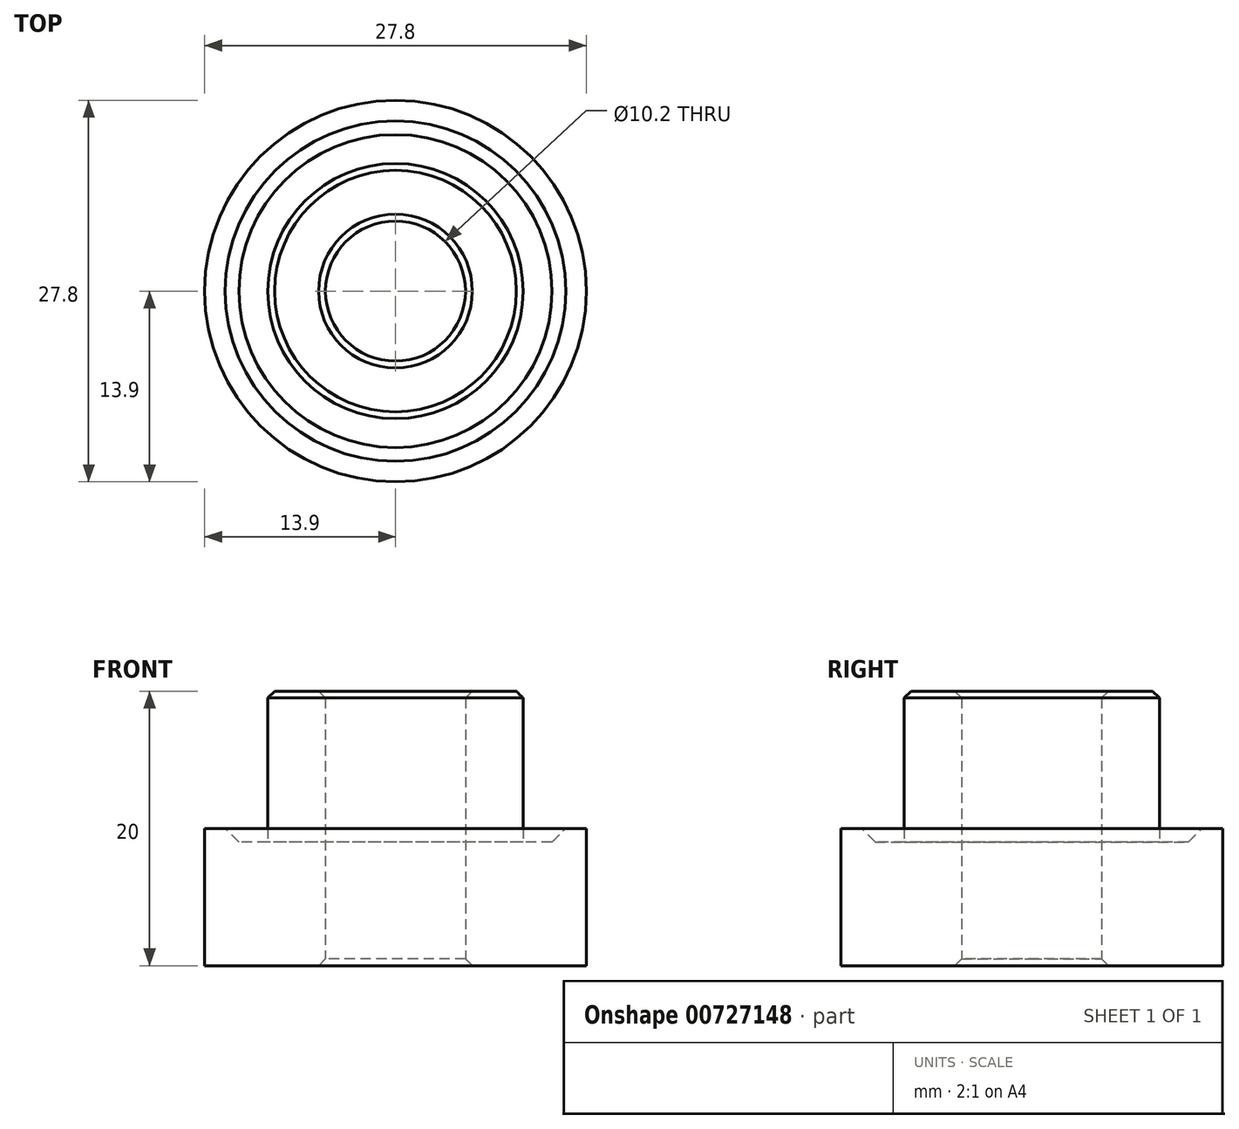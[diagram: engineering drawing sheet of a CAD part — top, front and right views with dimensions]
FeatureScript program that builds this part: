
annotation { "Feature Type Name" : "Feature", "Feature Type Description" : "" }
export const myFeature = defineFeature(function(context is Context, id is Id, definition is map)
    precondition{}
    {
        {
            var Q0;
            Q0=qCreatedBy(makeId("Top.planeOp"),FACE);
            var sketch = newSketch(context, id + "F0", { "sketchPlane" : qUnion([Q0])});
            skCircle(sketch, "E0", {"center": v(0, 0) * mm, "radius": 5.1 * mm});
            skCircle(sketch, "E1", {"center": v(0, 0) * mm, "radius": 9.3 * mm});
            skCircle(sketch, "E2", {"center": v(0, 0) * mm, "radius": 12.4 * mm});
            skCircle(sketch, "E3", {"center": v(0, 0) * mm, "radius": 13.9 * mm});
            skSolve(sketch);
        }
        {
            var Q0;
            Q0 = qSketchRegion(id + "F0", true);
            extrude(context, id + "F1", {"entities" : qUnion([Q0]), "depth" : 10 * mm, "offsetDistance" : 25 * mm});
        }
        {
            var Q0;
            Q0 = qSketchRegion(id + "F0", true);
            var Q1;
            Q1=makeQuery(id+"F0.imprint","IMPRINT",FACE,{"disambiguationData":[TD([[makeQuery(id+"F0.imprint","IMPRINT",EDGE,{"derivedFrom":sQuery(id+"F0.wireOp",EDGE,"E1")}),-1.0]])]});
            extrude(context, id + "F2", {"entities" : qUnion([Q0, Q1]), "operationType" : NewBodyOperationType.ADD, "depth" : 9 * mm, "offsetDistance" : 25 * mm});
        }
        {
            var Q0;
            Q0=makeQuery(id+"F0.imprint","IMPRINT",FACE,{"disambiguationData":[TD([[makeQuery(id+"F0.imprint","IMPRINT",EDGE,{"derivedFrom":sQuery(id+"F0.wireOp",EDGE,"E0")}),-1.0]])]});
            extrude(context, id + "F3", {"entities" : qUnion([Q0]), "operationType" : NewBodyOperationType.ADD, "depth" : 20 * mm, "offsetDistance" : 25 * mm});
        }
        {
            var Q0;
            Q0=makeQuery(id+"F3.opExtrude","CAP_EDGE",EDGE,{"disambiguationData":[OSD([sQuery(id+"F0.wireOp",EDGE,"E0")])],"isStart":false});
            var Q1;
            Q1=makeQuery(id+"F3.opExtrude","CAP_EDGE",EDGE,{"disambiguationData":[OSD([sQuery(id+"F0.wireOp",EDGE,"E1")])],"isStart":false});
            var Q2;
            Q2=makeQuery(id+"F2.opExtrude","CAP_EDGE",EDGE,{"disambiguationData":[OSD([sQuery(id+"F0.wireOp",EDGE,"E1")])],"isStart":false});
            var Q3;
            Q3=makeQuery(id+"F3.opExtrude","CAP_EDGE",EDGE,{"disambiguationData":[OSD([sQuery(id+"F0.wireOp",EDGE,"E0")])],"isStart":true});
            chamfer(context, id + "F4", {"entities" : qUnion([Q0, Q1, Q2, Q3]), "width" : 0.5 * mm, "tangentPropagation" : true});
        }
        {
            var Q0;
            Q0=makeQuery(id+"F2.boolean.opBoolean","INTERSECT",EDGE,{"derivedFrom":[makeQuery(id+"F1.opExtrude","SWEPT_FACE",FACE,{"disambiguationData":[OSD([sQuery(id+"F0.wireOp",EDGE,"E2")])]}),makeQuery(id+"F2.opExtrude","CAP_FACE",FACE,{"disambiguationData":[OSD([sQuery(id+"F0.wireOp",EDGE,"E1"),sQuery(id+"F0.wireOp",EDGE,"E3")])],"isStart":false})]});
            chamfer(context, id + "F5", {"entities" : qUnion([Q0]), "width" : 1 * mm, "tangentPropagation" : true});
        }
    });
